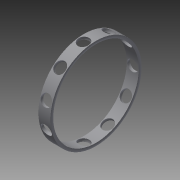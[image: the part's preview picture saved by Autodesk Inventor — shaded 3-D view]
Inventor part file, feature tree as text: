
AUTODESK INVENTOR PART (.ipt)
format: ipt  version: 2014 SP2 (Build 180246200, 246)  size: 240,128 bytes
history: native  units: mm
features: other x84, revolve x2, sketch x2, pattern_circular x1
ambient origin geometry x8: Origin, YZ Plane, XZ Plane, XY Plane, X Axis, Y Axis, Z Axis, Center Point
bodies: Solid1 (feature_tree)
feature tree (89):
  revolve  "Revolution1"  Angle=360.0deg
  revolve  "Revolution2"  [1 undecoded]
  pattern_circular  "Circular Pattern1"  [2 undecoded]
  other  "1_XY"
  other  "1_YZ"
  other  "1_ZX"
  other  "1_X"
  other  "1_Y"
  other  "1_Z"
  other  "1_Center"
  other  "2_1_XY"
  other  "2_1_YZ"
  other  "2_1_ZX"
  other  "2_1_X"
  other  "2_1_Y"
  other  "2_1_Z"
  other  "2_1_Center"
  other  "2_10_XY"
  other  "2_10_YZ"
  other  "2_10_ZX"
  other  "2_10_X"
  other  "2_10_Y"
  other  "2_10_Z"
  other  "2_10_Center"
  other  "2_11_XY"
  other  "2_11_YZ"
  other  "2_11_ZX"
  other  "2_11_X"
  other  "2_11_Y"
  other  "2_11_Z"
  other  "2_11_Center"
  other  "2_2_XY"
  other  "2_2_YZ"
  other  "2_2_ZX"
  other  "2_2_X"
  other  "2_2_Y"
  other  "2_2_Z"
  other  "2_2_Center"
  other  "2_3_XY"
  other  "2_3_YZ"
  other  "2_3_ZX"
  other  "2_3_X"
  other  "2_3_Y"
  other  "2_3_Z"
  other  "2_3_Center"
  other  "2_4_XY"
  other  "2_4_YZ"
  other  "2_4_ZX"
  other  "2_4_X"
  other  "2_4_Y"
  other  "2_4_Z"
  other  "2_4_Center"
  other  "2_5_XY"
  other  "2_5_YZ"
  other  "2_5_ZX"
  other  "2_5_X"
  other  "2_5_Y"
  other  "2_5_Z"
  other  "2_5_Center"
  other  "2_6_XY"
  other  "2_6_YZ"
  other  "2_6_ZX"
  other  "2_6_X"
  other  "2_6_Y"
  other  "2_6_Z"
  other  "2_6_Center"
  other  "2_7_XY"
  other  "2_7_YZ"
  other  "2_7_ZX"
  other  "2_7_X"
  other  "2_7_Y"
  other  "2_7_Z"
  other  "2_7_Center"
  other  "2_8_XY"
  other  "2_8_YZ"
  other  "2_8_ZX"
  other  "2_8_X"
  other  "2_8_Y"
  other  "2_8_Z"
  other  "2_8_Center"
  other  "2_9_XY"
  other  "2_9_YZ"
  other  "2_9_ZX"
  other  "2_9_X"
  other  "2_9_Y"
  other  "2_9_Z"
  other  "2_9_Center"
  sketch  "Sketch_6"  dims[d2=110.0mm d3=5.711987mm]
  sketch  "Sketch_2"  dims[d0=360.0deg d1=360.0deg]
note: 3 required parameter values undecoded (feature->parameter linkage not recoverable at this tier; creation-order binding heuristic only, values carry confidence <= 0.55)
